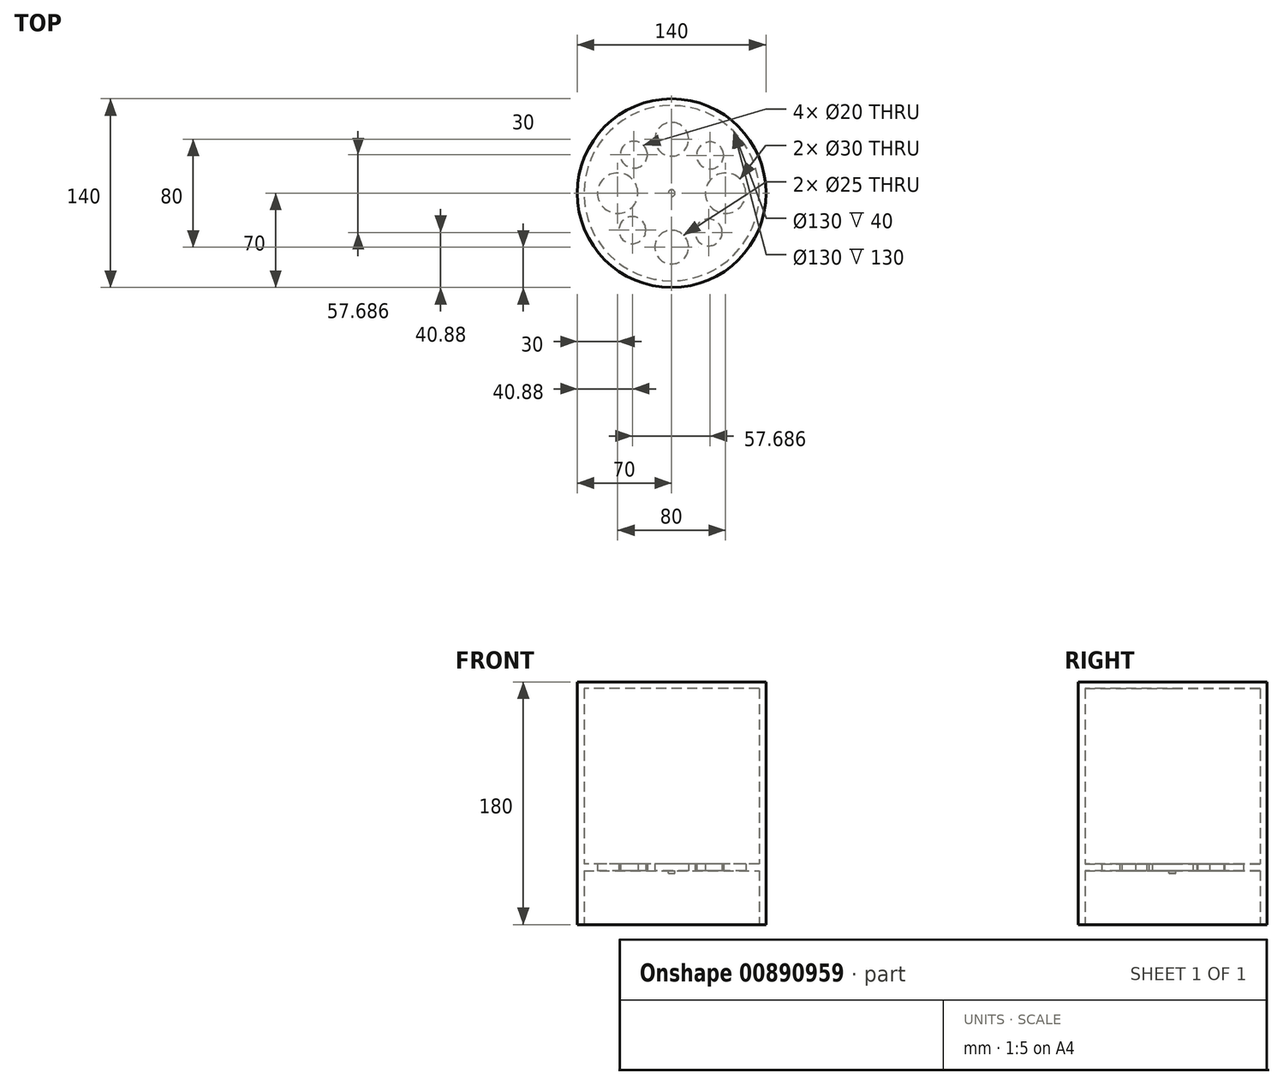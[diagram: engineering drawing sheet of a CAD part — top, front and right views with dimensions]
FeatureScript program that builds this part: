
annotation { "Feature Type Name" : "Feature", "Feature Type Description" : "" }
export const myFeature = defineFeature(function(context is Context, id is Id, definition is map)
    precondition{}
    {
        {
            var Q0;
            Q0=qCreatedBy(makeId("Top.planeOp"),FACE);
            var sketch = newSketch(context, id + "F0", { "sketchPlane" : qUnion([Q0])});
            skCircle(sketch, "E0", {"center": v(0, 0) * mm, "radius": 70 * mm});
            skSolve(sketch);
        }
        {
            var Q0;
            Q0 = qSketchRegion(id + "F0", true);
            extrude(context, id + "F1", {"entities" : qUnion([Q0]), "depth" : 180 * mm, "offsetDistance" : 25 * mm});
        }
        {
            var Q0;
            Q0=makeQuery(id+"F1.opExtrude","CAP_FACE",FACE,{"disambiguationData":[OSD([sQuery(id+"F0.wireOp",EDGE,"E0")])],"isStart":true});
            var sketch = newSketch(context, id + "F2", { "sketchPlane" : qUnion([Q0])});
            skCircle(sketch, "E1", {"center": v(0, 0) * mm, "radius": 65 * mm});
            skSolve(sketch);
        }
        {
            var Q0;
            Q0 = qSketchRegion(id + "F2", true);
            extrude(context, id + "F3", {"entities" : qUnion([Q0]), "operationType" : NewBodyOperationType.REMOVE, "oppositeDirection" : true, "depth" : 40 * mm, "offsetDistance" : 25 * mm});
        }
        {
            var Q0;
            Q0=qCreatedBy(makeId("Top.planeOp"),FACE);
            cPlane(context, id + "F4", {"entities" : qUnion([Q0]), "cplaneType" : CPlaneType.OFFSET, "offset" : 40 * mm, "width" : 150 * mm, "height" : 150 * mm});
        }
        {
            var Q0;
            Q0=qCreatedBy(id+"F4.planeOp",FACE);
            var sketch = newSketch(context, id + "F5", { "sketchPlane" : qUnion([Q0])});
            skCircle(sketch, "E2", {"center": v(40, 0) * mm, "radius": 15 * mm});
            skCircle(sketch, "E3.MirrorC", {"center": v(-40, 0) * mm, "radius": 15 * mm});
            skCircle(sketch, "E4", {"center": v(0, 40) * mm, "radius": 12.5 * mm});
            skCircle(sketch, "E5.MirrorC", {"center": v(0, -40) * mm, "radius": 12.5 * mm});
            skCircle(sketch, "E6", {"center": v(-28, 28.57) * mm, "radius": 10 * mm});
            skCircle(sketch, "E7.MirrorC", {"center": v(27.42, -29.12) * mm, "radius": 10 * mm});
            skCircle(sketch, "E8.MirrorC", {"center": v(-29.12, -27.42) * mm, "radius": 10 * mm});
            skCircle(sketch, "E9.MirrorC", {"center": v(28.57, 28) * mm, "radius": 10 * mm});
            skSolve(sketch);
        }
        {
            var Q0;
            Q0 = qSketchRegion(id + "F5", true);
            extrude(context, id + "F6", {"entities" : qUnion([Q0]), "operationType" : NewBodyOperationType.REMOVE, "depth" : 125 * mm, "offsetDistance" : 25 * mm});
        }
        {
            var Q0;
            Q0=qCreatedBy(makeId("Top.planeOp"),FACE);
            cPlane(context, id + "F7", {"entities" : qUnion([Q0]), "cplaneType" : CPlaneType.OFFSET, "offset" : 45 * mm, "width" : 150 * mm, "height" : 150 * mm});
        }
        {
            var Q0;
            Q0=qCreatedBy(id+"F7.planeOp",FACE);
            var sketch = newSketch(context, id + "F8", { "sketchPlane" : qUnion([Q0])});
            skCircle(sketch, "E10", {"center": v(0, 0) * mm, "radius": 65 * mm});
            skSolve(sketch);
        }
        {
            var Q0;
            Q0 = qSketchRegion(id + "F8", true);
            extrude(context, id + "F9", {"entities" : qUnion([Q0]), "operationType" : NewBodyOperationType.REMOVE, "depth" : 130 * mm, "offsetDistance" : 25 * mm});
        }
        {
            var Q0;
            Q0=makeQuery(id+"F3.boolean.opBoolean","COPY",FACE,{"derivedFrom":makeQuery(id+"F3.opExtrude","CAP_FACE",FACE,{"disambiguationData":[OSD([sQuery(id+"F2.wireOp",EDGE,"E1")])],"isStart":false})});
            var sketch = newSketch(context, id + "F10", { "sketchPlane" : qUnion([Q0])});
            skCircle(sketch, "E11", {"center": v(0, 0) * mm, "radius": 2.5 * mm});
            skSolve(sketch);
        }
        {
            var Q0;
            Q0 = qSketchRegion(id + "F10", true);
            extrude(context, id + "F11", {"entities" : qUnion([Q0]), "operationType" : NewBodyOperationType.ADD, "depth" : 2 * mm, "offsetDistance" : 25 * mm});
        }
    });
